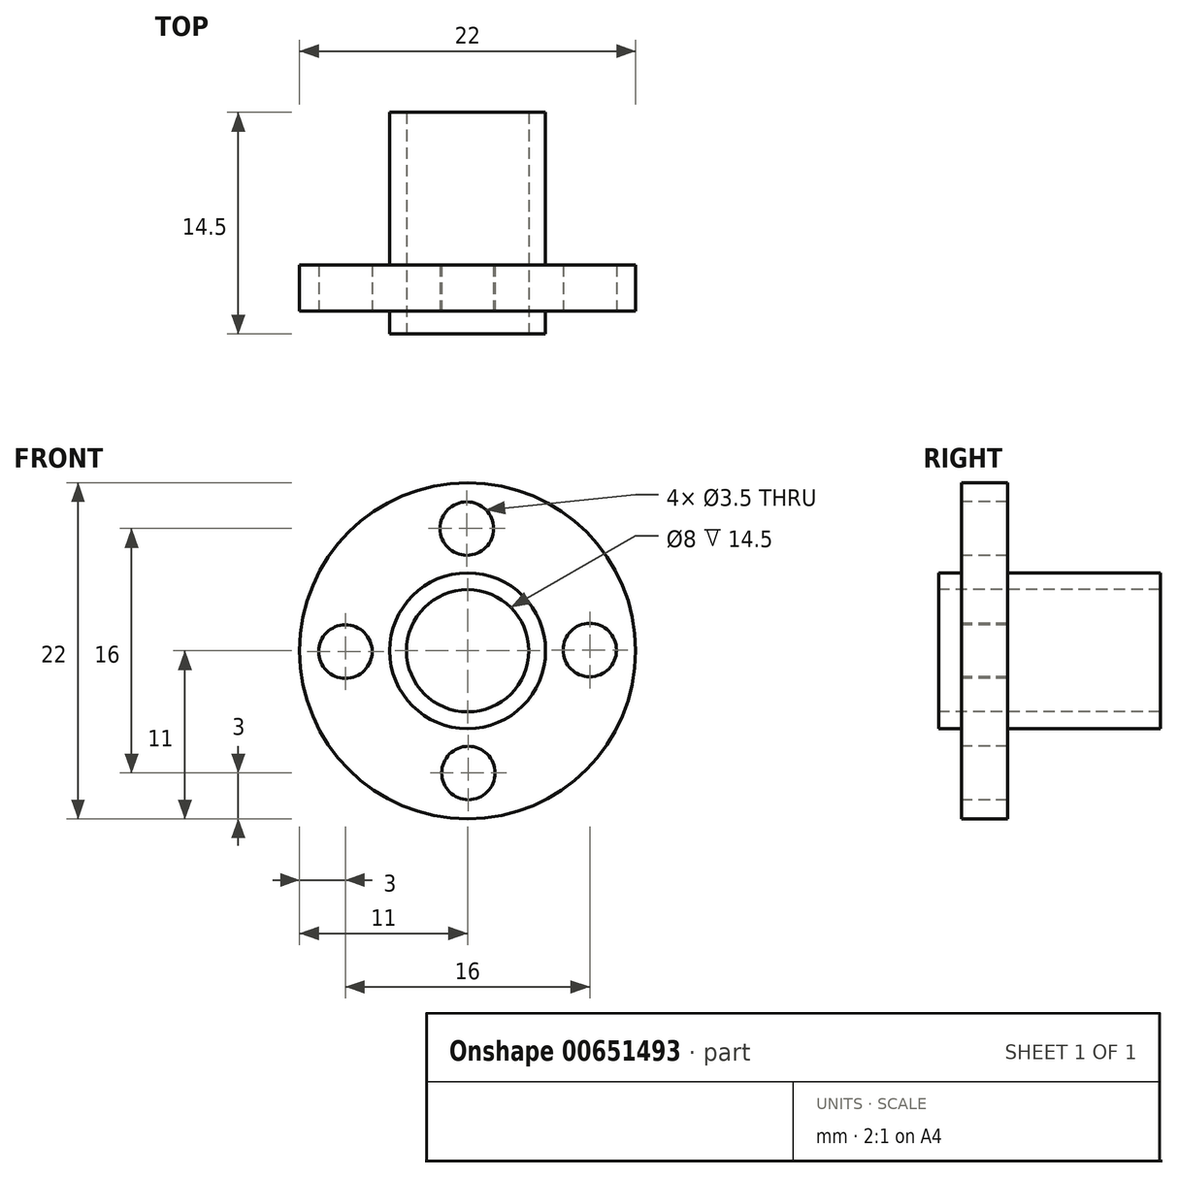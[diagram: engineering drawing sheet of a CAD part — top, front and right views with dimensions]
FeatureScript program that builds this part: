
annotation { "Feature Type Name" : "Feature", "Feature Type Description" : "" }
export const myFeature = defineFeature(function(context is Context, id is Id, definition is map)
    precondition{}
    {
        {
            var Q0;
            Q0=qCreatedBy(makeId("Front.planeOp"),FACE);
            var sketch = newSketch(context, id + "F0", { "sketchPlane" : qUnion([Q0])});
            skCircle(sketch, "E0", {"center": v(0, 0) * mm, "radius": 11 * mm});
            skSolve(sketch);
        }
        {
            var Q0;
            Q0=makeQuery(id+"F0.imprint","IMPRINT",FACE,{"disambiguationData":[TD([[makeQuery(id+"F0.imprint","IMPRINT",EDGE,{"derivedFrom":sQuery(id+"F0.wireOp",EDGE,"E0")}),1.0]])]});
            extrude(context, id + "F1", {"entities" : qUnion([Q0]), "depth" : 3 * mm, "offsetDistance" : 25 * mm});
        }
        {
            var Q0;
            Q0=makeQuery(id+"F1.opExtrude","CAP_FACE",FACE,{"disambiguationData":[OSD([sQuery(id+"F0.wireOp",EDGE,"E0")])],"isStart":false});
            var sketch = newSketch(context, id + "F2", { "sketchPlane" : qUnion([Q0])});
            skCircle(sketch, "E1", {"center": v(0, 0) * mm, "radius": 5.1 * mm});
            skSolve(sketch);
        }
        {
            var Q0;
            Q0=makeQuery(id+"F2.imprint","IMPRINT",FACE,{"disambiguationData":[TD([[makeQuery(id+"F2.imprint","IMPRINT",EDGE,{"derivedFrom":sQuery(id+"F2.wireOp",EDGE,"E1")}),1.0]])]});
            extrude(context, id + "F3", {"entities" : qUnion([Q0]), "operationType" : NewBodyOperationType.ADD, "depth" : 1.5 * mm, "offsetDistance" : 25 * mm, "hasSecondDirection" : true, "secondDirectionOppositeDirection" : true, "secondDirectionDepth" : 13 * mm});
        }
        {
            var Q0;
            Q0=makeQuery(id+"F3.opExtrude","CAP_FACE",FACE,{"disambiguationData":[OSD([sQuery(id+"F2.wireOp",EDGE,"E1")])],"isStart":false});
            var sketch = newSketch(context, id + "F4", { "sketchPlane" : qUnion([Q0])});
            skCircle(sketch, "E2", {"center": v(0, 0) * mm, "radius": 4 * mm});
            skSolve(sketch);
        }
        {
            var Q0;
            Q0 = qSketchRegion(id + "F4", true);
            extrude(context, id + "F5", {"entities" : qUnion([Q0]), "operationType" : NewBodyOperationType.REMOVE, "oppositeDirection" : true, "depth" : 25 * mm, "offsetDistance" : 25 * mm});
        }
        {
            var Q0;
            Q0=makeQuery(id+"F1.opExtrude","CAP_FACE",FACE,{"disambiguationData":[OSD([sQuery(id+"F0.wireOp",EDGE,"E0")])],"isStart":false});
            var sketch = newSketch(context, id + "F6", { "sketchPlane" : qUnion([Q0])});
            skCircle(sketch, "E3", {"center": v(0, 0) * mm, "radius": 8 * mm, "construction": true});
            skCircle(sketch, "E4", {"center": v(-0.05, 8) * mm, "radius": 1.75 * mm});
            skCircle(sketch, "E5.1.0", {"center": v(-8, -0.05) * mm, "radius": 1.75 * mm});
            skCircle(sketch, "E5.2.0", {"center": v(0.05, -8) * mm, "radius": 1.75 * mm});
            skCircle(sketch, "E5.3.0", {"center": v(8, 0.05) * mm, "radius": 1.75 * mm});
            skSolve(sketch);
        }
        {
            var Q0;
            Q0=makeQuery(id+"F6.imprint","IMPRINT",FACE,{"disambiguationData":[TD([[makeQuery(id+"F6.imprint","IMPRINT",EDGE,{"derivedFrom":sQuery(id+"F6.wireOp",EDGE,"E4")}),1.0]])]});
            var Q1;
            Q1=makeQuery(id+"F6.imprint","IMPRINT",FACE,{"disambiguationData":[TD([[makeQuery(id+"F6.imprint","IMPRINT",EDGE,{"derivedFrom":sQuery(id+"F6.wireOp",EDGE,"E5.3.0")}),1.0]])]});
            var Q2;
            Q2=makeQuery(id+"F6.imprint","IMPRINT",FACE,{"disambiguationData":[TD([[makeQuery(id+"F6.imprint","IMPRINT",EDGE,{"derivedFrom":sQuery(id+"F6.wireOp",EDGE,"E5.2.0")}),1.0]])]});
            var Q3;
            Q3=makeQuery(id+"F6.imprint","IMPRINT",FACE,{"disambiguationData":[TD([[makeQuery(id+"F6.imprint","IMPRINT",EDGE,{"derivedFrom":sQuery(id+"F6.wireOp",EDGE,"E5.1.0")}),1.0]])]});
            extrude(context, id + "F7", {"entities" : qUnion([Q0, Q1, Q2, Q3]), "operationType" : NewBodyOperationType.REMOVE, "oppositeDirection" : true, "depth" : 25 * mm, "offsetDistance" : 25 * mm});
        }
    });
